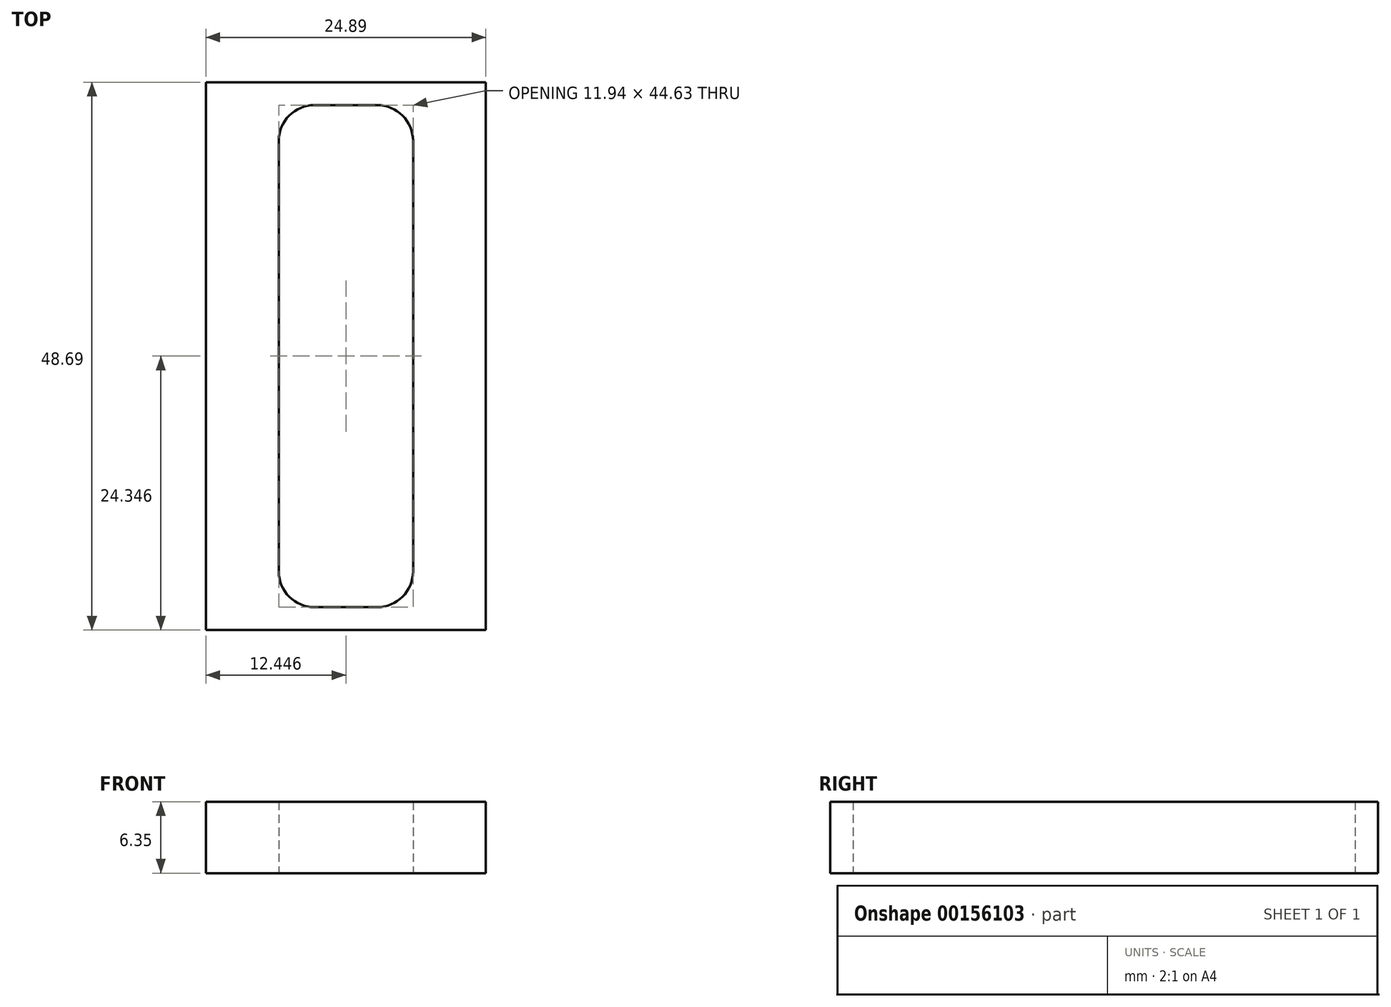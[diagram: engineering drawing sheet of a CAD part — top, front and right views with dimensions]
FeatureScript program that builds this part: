
annotation { "Feature Type Name" : "Feature", "Feature Type Description" : "" }
export const myFeature = defineFeature(function(context is Context, id is Id, definition is map)
    precondition{}
    {
        {
            var Q0;
            Q0=qCreatedBy(makeId("Top.planeOp"),FACE);
            var sketch = newSketch(context, id + "F0", { "sketchPlane" : qUnion([Q0])});
            skLineSegment(sketch, "E0.bottom", {"start": v(0, 0) * mm, "end": v(24.9, 0) * mm});
            skLineSegment(sketch, "E0.top", {"start": v(0, 48.7) * mm, "end": v(24.9, 48.7) * mm});
            skLineSegment(sketch, "E0.left", {"start": v(0, 0) * mm, "end": v(0, 48.7) * mm});
            skLineSegment(sketch, "E0.right", {"start": v(24.9, 0) * mm, "end": v(24.9, 48.7) * mm});
            skLineSegment(sketch, "E1.bottom", {"start": v(9.65, 46.66) * mm, "end": v(15.24, 46.66) * mm});
            skLineSegment(sketch, "E1.top", {"start": v(9.65, 2.03) * mm, "end": v(15.24, 2.03) * mm});
            skLineSegment(sketch, "E1.left", {"start": v(6.48, 43.48) * mm, "end": v(6.48, 5.2) * mm});
            skLineSegment(sketch, "E1.right", {"start": v(18.41, 43.48) * mm, "end": v(18.41, 5.2) * mm});
            skPoint(sketch, "E2.visualSharp", {"position": v(6.48, 46.66) * mm});
            skArc(sketch, "E2.filletArc", {"start": v(9.65, 46.66) * mm, "mid": v(7.4, 45.73) * mm, "end": v(6.48, 43.48) * mm});
            skPoint(sketch, "E3.visualSharp", {"position": v(18.41, 46.66) * mm});
            skArc(sketch, "E3.filletArc", {"start": v(18.41, 43.48) * mm, "mid": v(17.49, 45.73) * mm, "end": v(15.24, 46.66) * mm});
            skPoint(sketch, "E4.visualSharp", {"position": v(18.41, 2.03) * mm});
            skArc(sketch, "E4.filletArc", {"start": v(15.24, 2.03) * mm, "mid": v(17.49, 2.96) * mm, "end": v(18.41, 5.2) * mm});
            skPoint(sketch, "E5.visualSharp", {"position": v(6.48, 2.03) * mm});
            skArc(sketch, "E5.filletArc", {"start": v(6.48, 5.2) * mm, "mid": v(7.4, 2.96) * mm, "end": v(9.65, 2.03) * mm});
            skSolve(sketch);
        }
        {
            var Q0;
            Q0 = qSketchRegion(id + "F0", true);
            extrude(context, id + "F1", {"entities" : qUnion([Q0]), "depth" : 6.35 * mm});
        }
    });
